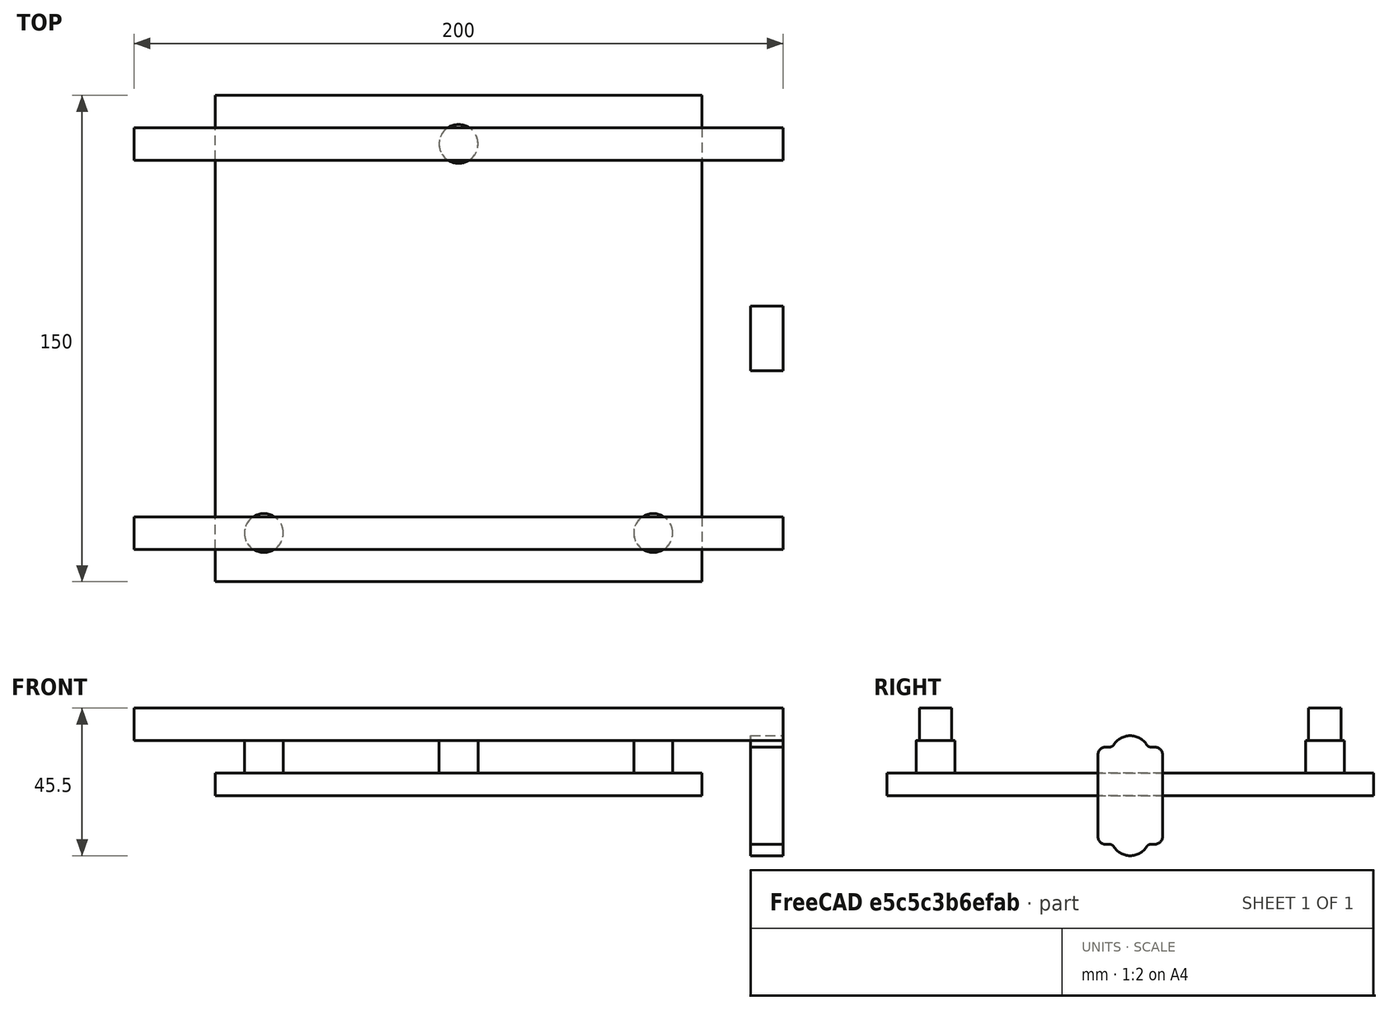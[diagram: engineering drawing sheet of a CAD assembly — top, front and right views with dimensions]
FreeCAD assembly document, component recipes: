
FREECAD ASSEMBLY — COMPONENT RECIPES ("miniXY-PrintBed")

This assembly document has 2 components, labeled P0..P1 below (a component is one placed body or linked part). 2 of them carry a construction recipe — the FreeCAD feature program that regenerates the part from scratch, quoted from this document or its linked companion documents; the rest are supplied as boundary geometry only. No exploded tour is included for this assembly.
COMPONENT P0 — recipe-attached ("PrintBed", modeled in this document).
Construction recipe (the document's own serialized feature program — sketch geometry with constraints, then the solid features built on it; lengths are millimeters unless a unit is written):

FEATURE [Sketcher::SketchObject] Sketch
  FullyConstrained = true
  MapMode = 5
  Support = -> [XY_Plane002]
  expr: Constraints[10] = <<Variables>>.BedSize
  sketch-geometry (4):
    g0: LineSegment StartX=-75 StartY=75 StartZ=0 EndX=75 EndY=75 EndZ=0
    g1: LineSegment StartX=75 StartY=75 StartZ=0 EndX=75 EndY=-75 EndZ=0
    g2: LineSegment StartX=75 StartY=-75 StartZ=0 EndX=-75 EndY=-75 EndZ=0
    g3: LineSegment StartX=-75 StartY=-75 StartZ=0 EndX=-75 EndY=75 EndZ=0
  constraints (11):
    c: Coincident(g0,g1)
    c: Coincident(g1,g2)
    c: Coincident(g2,g3)
    c: Coincident(g3,g0)
    c: Horizontal(g0)
    c: Horizontal(g2)
    c: Vertical(g1)
    c: Vertical(g3)
    c: Symmetric(g0,g1,g-1)
    c: Equal(g0,g3)
    c: Distance(g3) = 150
FEATURE [PartDesign::Pad] Pad
  Direction = (0,0,1)
  Length = 7
  Length2 = 10
  Profile = -> Sketch
  ReferenceAxis = -> Sketch [N_Axis]
  Type = 0
  expr: Length = <<Variables>>.BedThickness
FEATURE [PartDesign::Body] Body  label="Bed"
  Group = -> [Sketch,Pad]
  Origin = -> Origin002
  Tip = -> Pad
FEATURE [Sketcher::SketchObject] Sketch001
  AttachmentOffset = pos=(0,0,7) rot=(0,0,1;0rad)
  FullyConstrained = false
  MapMode = 5
  Placement = pos=(0,0,7) rot=(0,0,1;0rad)
  Support = -> [XY_Plane003]
  expr: .AttachmentOffset.Base.z = <<Variables>>.BedThickness
  expr: Constraints[12] = <<Variables>>.BedSize / 2 - 15
  expr: Constraints[9] = <<Variables>>.BedSize
  sketch-geometry (5):
    g0: LineSegment StartX=-75 StartY=58.3105 StartZ=0 EndX=75 EndY=58.3105 EndZ=0
    g1: LineSegment StartX=75 StartY=58.3105 StartZ=0 EndX=75 EndY=-58.3105 EndZ=0
    g2: LineSegment StartX=75 StartY=-58.3105 StartZ=0 EndX=-75 EndY=-58.3105 EndZ=0
    g3: LineSegment StartX=-75 StartY=-58.3105 StartZ=0 EndX=-75 EndY=91.6895 EndZ=0
    g4: Circle CenterX=0 CenterY=60 CenterZ=0 NormalX=0 NormalY=0 NormalZ=1 AngleXU=0 Radius=6
  constraints (13):
    c: Coincident(g0,g1)
    c: Coincident(g1,g2)
    c: Coincident(g2,g3)
    c: Horizontal(g0)
    c: Horizontal(g2)
    c: Vertical(g1)
    c: Vertical(g3)
    c: Symmetric(g0,g1,g-1)
    c: Equal(g0,g3)
    c: Distance(g3) = 150
    c: PointOnObject(g4,g-2)
    c: Diameter(g4) = 12
    c: DistanceY(g4) = 60
FEATURE [Sketcher::SketchObject] Sketch002
  AttachmentOffset = pos=(0,0,7) rot=(0,0,1;0rad)
  FullyConstrained = true
  MapMode = 5
  Placement = pos=(0,0,7) rot=(0,0,1;0rad)
  Support = -> [XY_Plane004]
  expr: .AttachmentOffset.Base.z = <<Variables>>.BedThickness
  expr: Constraints[10] = <<Variables>>.BedSize
  expr: Constraints[11] = -(<<Variables>>.BedSize / 2 - 15)
  expr: Constraints[12] = -(<<Variables>>.BedSize / 2 - 15)
  sketch-geometry (5):
    g0: LineSegment StartX=-75 StartY=75 StartZ=0 EndX=75 EndY=75 EndZ=0
    g1: LineSegment StartX=75 StartY=75 StartZ=0 EndX=75 EndY=-75 EndZ=0
    g2: LineSegment StartX=75 StartY=-75 StartZ=0 EndX=-75 EndY=-75 EndZ=0
    g3: LineSegment StartX=-75 StartY=-75 StartZ=0 EndX=-75 EndY=75 EndZ=0
    g4: Circle CenterX=-60 CenterY=-60 CenterZ=0 NormalX=0 NormalY=0 NormalZ=1 AngleXU=0 Radius=6
  constraints (14):
    c: Coincident(g0,g1)
    c: Coincident(g1,g2)
    c: Coincident(g2,g3)
    c: Coincident(g3,g0)
    c: Horizontal(g0)
    c: Horizontal(g2)
    c: Vertical(g1)
    c: Vertical(g3)
    c: Symmetric(g1,g0,g-1)
    c: Equal(g0,g3)
    c: Distance(g3) = 150
    c: DistanceY(g4) = -60
    c: DistanceX(g4) = -60
    c: Diameter(g4) = 12
FEATURE [Sketcher::SketchObject] Sketch003
  AttachmentOffset = pos=(0,0,7) rot=(0,0,1;0rad)
  FullyConstrained = true
  MapMode = 5
  Placement = pos=(0,0,7) rot=(0,0,1;0rad)
  Support = -> [XY_Plane005]
  expr: .AttachmentOffset.Base.z = <<Variables>>.BedThickness
  expr: Constraints[10] = <<Variables>>.BedSize
  expr: Constraints[11] = <<Variables>>.BedSize / 2 - 15
  expr: Constraints[12] = -(<<Variables>>.BedSize / 2 - 15)
  sketch-geometry (5):
    g0: LineSegment StartX=-75 StartY=75 StartZ=0 EndX=75 EndY=75 EndZ=0
    g1: LineSegment StartX=75 StartY=75 StartZ=0 EndX=75 EndY=-75 EndZ=0
    g2: LineSegment StartX=75 StartY=-75 StartZ=0 EndX=-75 EndY=-75 EndZ=0
    g3: LineSegment StartX=-75 StartY=-75 StartZ=0 EndX=-75 EndY=75 EndZ=0
    g4: Circle CenterX=60 CenterY=-60 CenterZ=0 NormalX=0 NormalY=0 NormalZ=1 AngleXU=0 Radius=6
  constraints (14):
    c: Coincident(g0,g1)
    c: Coincident(g1,g2)
    c: Coincident(g2,g3)
    c: Coincident(g3,g0)
    c: Horizontal(g0)
    c: Horizontal(g2)
    c: Vertical(g1)
    c: Vertical(g3)
    c: Symmetric(g0,g1,g-1)
    c: Equal(g0,g3)
    c: Distance(g3) = 150
    c: DistanceX(g4) = 60
    c: DistanceY(g4) = -60
    c: Diameter(g4) = 12
FEATURE [PartDesign::Pad] Pad001
  Direction = (0,0,1)
  Length = 10
  Length2 = 10
  Profile = -> Sketch001
  ReferenceAxis = -> Sketch001 [N_Axis]
  Type = 0
FEATURE [PartDesign::Body] Body001  label="BootRear"
  Group = -> [Sketch001,Pad001]
  Origin = -> Origin003
  Tip = -> Pad001
FEATURE [PartDesign::Pad] Pad002
  Direction = (0,0,1)
  Length = 10
  Length2 = 10
  Profile = -> Sketch002
  ReferenceAxis = -> Sketch002 [N_Axis]
  Type = 0
FEATURE [PartDesign::Body] Body002  label="BootFrontLeft"
  Group = -> [Sketch002,Pad002]
  Origin = -> Origin004
  Tip = -> Pad002
FEATURE [PartDesign::Pad] Pad003
  Direction = (0,0,1)
  Length = 10
  Length2 = 10
  Profile = -> Sketch003
  ReferenceAxis = -> Sketch003 [N_Axis]
  Type = 0
FEATURE [PartDesign::Body] Body003  label="BootFrontRight"
  Group = -> [Sketch003,Pad003]
  Origin = -> Origin005
  Tip = -> Pad003
FEATURE [Sketcher::SketchObject] Sketch004
  FullyConstrained = true
  MapMode = 5
  Placement = pos=(0,0,0) rot=(0.57735,0.57735,0.57735;2.0944rad)
  Support = -> [YZ_Plane006]
  expr: Constraints[11] = -(<<Variables>>.BedSize / 2 - 15)
  expr: Constraints[12] = 10 + <<Variables>>.BedThickness
  sketch-geometry (5):
    g0: LineSegment StartX=-65 StartY=27 StartZ=0 EndX=-55 EndY=27 EndZ=0
    g1: LineSegment StartX=-55 StartY=27 StartZ=0 EndX=-55 EndY=17 EndZ=0
    g2: LineSegment StartX=-55 StartY=17 StartZ=0 EndX=-65 EndY=17 EndZ=0
    g3: LineSegment StartX=-65 StartY=17 StartZ=0 EndX=-65 EndY=27 EndZ=0
    g4: GeomPoint X=-60 Y=22 Z=0
  constraints (13):
    c: Coincident(g0,g1)
    c: Coincident(g1,g2)
    c: Coincident(g2,g3)
    c: Coincident(g3,g0)
    c: Horizontal(g0)
    c: Horizontal(g2)
    c: Vertical(g1)
    c: Vertical(g3)
    c: Equal(g0,g3)
    c: Distance(g3) = 10
    c: Symmetric(g0,g1,g4)
    c: DistanceX(g4) = -60
    c: DistanceY(g2) = 17
FEATURE [PartDesign::Pad] Pad004
  Direction = (1,-2e-16,3e-16)
  Length = 200
  Length2 = 10
  Midplane = true
  Placement = pos=(0,0,0) rot=(0.57735,0.57735,0.57735;2.0944rad)
  Profile = -> Sketch004
  ReferenceAxis = -> Sketch004 [N_Axis]
  Type = 0
  expr: Length = Variables.GantorySpacing
FEATURE [PartDesign::Body] Body004  label="FrameFront"
  Group = -> [Sketch004,Pad004]
  Origin = -> Origin006
  Tip = -> Pad004
FEATURE [Sketcher::SketchObject] Sketch005
  FullyConstrained = true
  MapMode = 5
  Placement = pos=(0,0,0) rot=(0.57735,0.57735,0.57735;2.0944rad)
  Support = -> [YZ_Plane007]
  expr: Constraints[11] = <<Variables>>.BedSize / 2 - 15
  expr: Constraints[12] = 10 + <<Variables>>.BedThickness
  sketch-geometry (5):
    g0: LineSegment StartX=55 StartY=27 StartZ=0 EndX=65 EndY=27 EndZ=0
    g1: LineSegment StartX=65 StartY=27 StartZ=0 EndX=65 EndY=17 EndZ=0
    g2: LineSegment StartX=65 StartY=17 StartZ=0 EndX=55 EndY=17 EndZ=0
    g3: LineSegment StartX=55 StartY=17 StartZ=0 EndX=55 EndY=27 EndZ=0
    g4: GeomPoint X=60 Y=22 Z=0
  constraints (13):
    c: Coincident(g0,g1)
    c: Coincident(g1,g2)
    c: Coincident(g2,g3)
    c: Coincident(g3,g0)
    c: Horizontal(g0)
    c: Horizontal(g2)
    c: Vertical(g1)
    c: Vertical(g3)
    c: Symmetric(g0,g1,g4)
    c: Equal(g0,g3)
    c: Distance(g3) = 10
    c: DistanceX(g4) = 60
    c: DistanceY(g2) = 17
FEATURE [PartDesign::Pad] Pad005
  Direction = (1,-2e-16,3e-16)
  Length = 200
  Length2 = 10
  Midplane = true
  Placement = pos=(0,0,0) rot=(0.57735,0.57735,0.57735;2.0944rad)
  Profile = -> Sketch005
  ReferenceAxis = -> Sketch005 [N_Axis]
  Type = 0
  expr: Length = <<Variables>>.GantorySpacing
FEATURE [PartDesign::Body] Body005  label="FrameRear"
  Group = -> [Sketch005,Pad005]
  Origin = -> Origin007
  Tip = -> Pad005
COMPONENT P1 — recipe-attached ("CarriageLeft", modeled in this document).
Construction recipe (the document's own serialized feature program — sketch geometry with constraints, then the solid features built on it; lengths are millimeters unless a unit is written):

FEATURE [Sketcher::SketchObject] Sketch006
  AttachmentOffset = pos=(0,0,100) rot=(0,0,1;0rad)
  FullyConstrained = true
  MapMode = 5
  Placement = pos=(100,-2.22e-14,2.22e-14) rot=(0.57735,0.57735,0.57735;2.0944rad)
  Support = -> [YZ_Plane008]
  expr: .AttachmentOffset.Base.z = Variables.GantorySpacing / 2
  sketch-geometry (20):
    g0: LineSegment StartX=10 StartY=12.5 StartZ=0 EndX=10 EndY=-12.5 EndZ=0
    g1: LineSegment StartX=-10 StartY=-12.5 StartZ=0 EndX=-10 EndY=12.5 EndZ=0
    g2: ArcOfCircle CenterX=-7.5 CenterY=12.5 CenterZ=0 NormalX=0 NormalY=0 NormalZ=1 AngleXU=0 Radius=2.5 StartAngle=1.5708 EndAngle=3.14159
    g3: GeomPoint X=-10 Y=15 Z=0
    g4: ArcOfCircle CenterX=-7.5 CenterY=-12.5 CenterZ=0 NormalX=0 NormalY=0 NormalZ=1 AngleXU=0 Radius=2.5 StartAngle=3.14159 EndAngle=4.71239
    g5: GeomPoint X=-10 Y=-15 Z=0
    g6: ArcOfCircle CenterX=7.5 CenterY=-12.5 CenterZ=0 NormalX=0 NormalY=0 NormalZ=1 AngleXU=0 Radius=2.5 StartAngle=4.71239 EndAngle=6.28319
    g7: GeomPoint X=10 Y=-15 Z=0
    g8: ArcOfCircle CenterX=7.5 CenterY=12.5 CenterZ=0 NormalX=0 NormalY=0 NormalZ=1 AngleXU=0 Radius=2.5 StartAngle=0 EndAngle=1.5708
    g9: GeomPoint X=10 Y=15 Z=0
    g10: ArcOfCircle CenterX=0 CenterY=12.5 CenterZ=0 NormalX=0 NormalY=0 NormalZ=1 AngleXU=0 Radius=6 StartAngle=0.562536 EndAngle=2.57906
    g11: ArcOfCircle CenterX=-6.34429 CenterY=16.5 CenterZ=0 NormalX=0 NormalY=0 NormalZ=1 AngleXU=0 Radius=1.5 StartAngle=4.71239 EndAngle=5.72065
    g12: ArcOfCircle CenterX=6.34429 CenterY=16.5 CenterZ=0 NormalX=0 NormalY=0 NormalZ=1 AngleXU=0 Radius=1.5 StartAngle=3.70413 EndAngle=4.71239
    g13: ArcOfCircle CenterX=0 CenterY=-12.5 CenterZ=0 NormalX=0 NormalY=0 NormalZ=1 AngleXU=0 Radius=6 StartAngle=3.70413 EndAngle=5.72065
    g14: ArcOfCircle CenterX=-6.34429 CenterY=-16.5 CenterZ=0 NormalX=0 NormalY=0 NormalZ=1 AngleXU=0 Radius=1.5 StartAngle=0.562536 EndAngle=1.5708
    g15: ArcOfCircle CenterX=6.34429 CenterY=-16.5 CenterZ=0 NormalX=0 NormalY=0 NormalZ=1 AngleXU=0 Radius=1.5 StartAngle=1.5708 EndAngle=2.57906
    g16: LineSegment StartX=-7.5 StartY=15 StartZ=0 EndX=-6.34429 EndY=15 EndZ=0
    g17: LineSegment StartX=6.34429 StartY=15 StartZ=0 EndX=7.5 EndY=15 EndZ=0
    g18: LineSegment StartX=-6.34429 StartY=-15 StartZ=0 EndX=-7.5 EndY=-15 EndZ=0
    g19: LineSegment StartX=7.5 StartY=-15 StartZ=0 EndX=6.34429 EndY=-15 EndZ=0
  constraints (46):
    c: Vertical(g0)
    c: Vertical(g1)
    c: Symmetric(g3,g7,g-1)
    c: PointOnObject(g3,g1)
    c: Tangent(g16,g2) = 1.5708
    c: Tangent(g1,g2) = 1.5708
    c: PointOnObject(g5,g1)
    c: Tangent(g1,g4) = 1.5708
    c: Tangent(g18,g4) = 1.5708
    c: PointOnObject(g7,g0)
    c: Tangent(g19,g6) = 1.5708
    c: Tangent(g0,g6) = 1.5708
    c: PointOnObject(g9,g0)
    c: Tangent(g0,g8) = 1.5708
    c: Tangent(g17,g8) = 1.5708
    c: Equal(g2,g4)
    c: Radius(g2) = 2.5
    c: Tangent(g10,g11) = 1.5708
    c: Tangent(g10,g12) = 1.5708
    c: PointOnObject(g10,g-2)
    c: Horizontal(g16)
    c: PointOnObject(g3,g16)
    c: Horizontal(g17)
    c: PointOnObject(g9,g17)
    c: Tangent(g11,g16) = -1.5708
    c: Tangent(g12,g17) = -1.5708
    c: Diameter(g10) = 12
    c: Equal(g11,g12)
    c: Diameter(g11) = 3
    c: Tangent(g14,g13) = 1.5708
    c: Tangent(g13,g15) = 1.5708
    c: Horizontal(g18)
    c: PointOnObject(g5,g18)
    c: Horizontal(g19)
    c: PointOnObject(g7,g19)
    c: Tangent(g14,g18) = -1.5708
    c: Symmetric(g13,g10,g-1)
    c: Tangent(g15,g19) = -1.5708
    c: Equal(g14,g11)
    c: Equal(g15,g11)
    c: Equal(g13,g10)
    c: DistanceY(g5,g3) = 30
    c: DistanceX(g3,g9) = 20
    c: Symmetric(g2,g8,g-2)
    c: Symmetric(g6,g4,g-2)
    c: DistanceY(g13,g10) = 25
FEATURE [PartDesign::Pad] Pad006
  Direction = (1,-2e-16,3e-16)
  Length = 10
  Length2 = 10
  Placement = pos=(0,0,0) rot=(0.57735,0.57735,0.57735;2.0944rad)
  Profile = -> Sketch006
  ReferenceAxis = -> Sketch006 [N_Axis]
  Reversed = true
  Type = 0
FEATURE [PartDesign::Body] Body006  label="CarriageLeftBase"
  Group = -> [Sketch006,Pad006]
  Origin = -> Origin008
  Tip = -> Pad006
PROVENANCE & LICENSES
A FreeCAD (.FCStd) document from a public repository crawl; recipes are the document's own serialized feature recipes (and, for linked parts, companion documents' recipes).
License: gpl-3.0.
